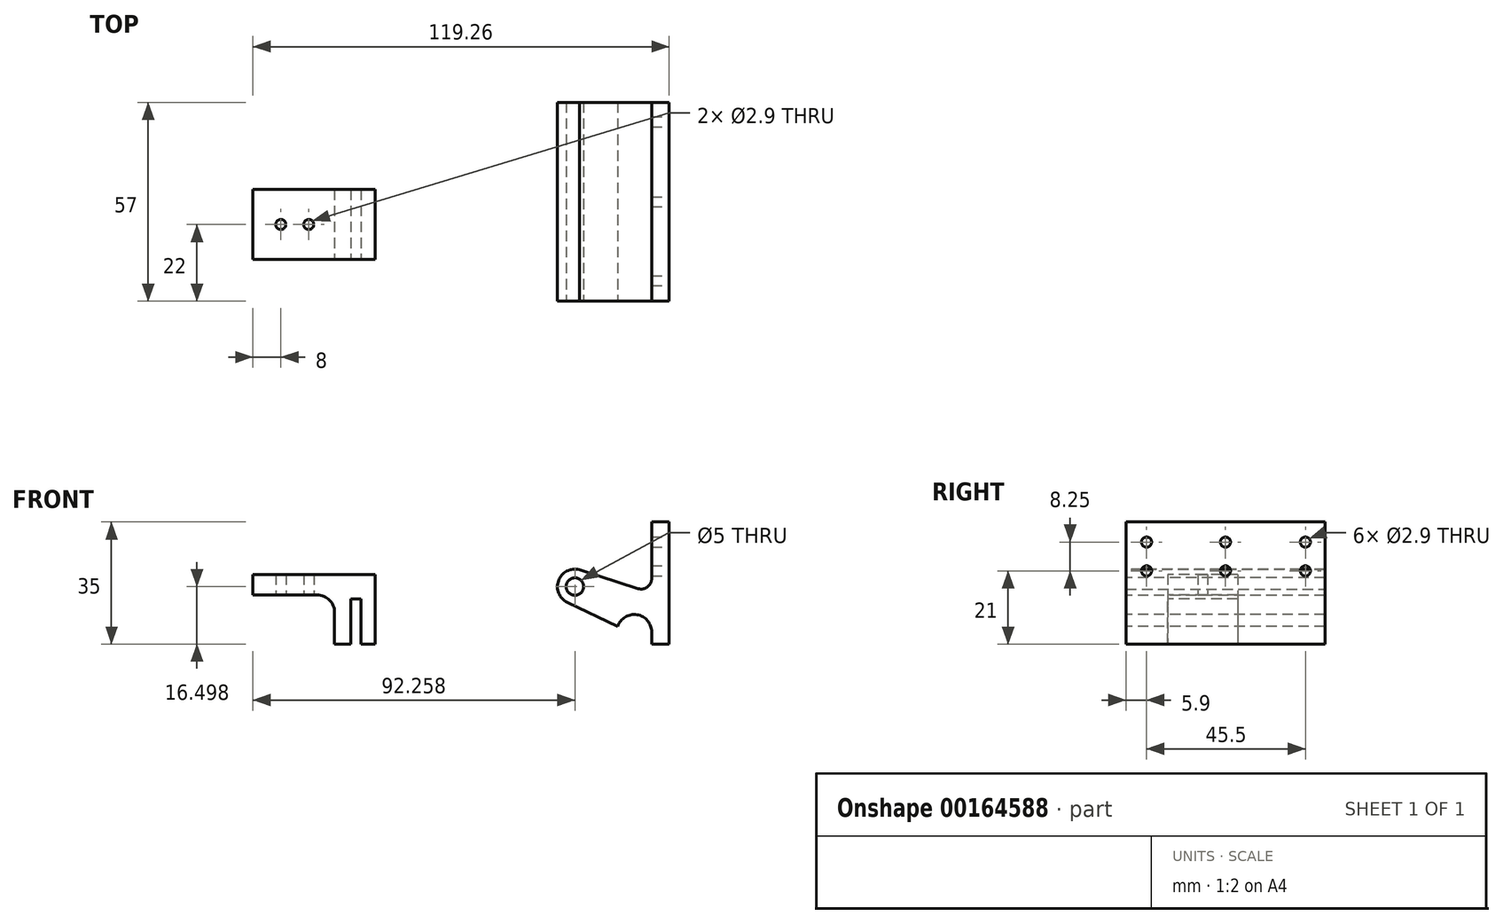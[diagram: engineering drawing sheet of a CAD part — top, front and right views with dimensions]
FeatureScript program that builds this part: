
annotation { "Feature Type Name" : "Feature", "Feature Type Description" : "" }
export const myFeature = defineFeature(function(context is Context, id is Id, definition is map)
    precondition{}
    {
        {
            var Q0;
            Q0=qCreatedBy(makeId("Top.planeOp"),FACE);
            var sketch = newSketch(context, id + "F0", { "sketchPlane" : qUnion([Q0])});
            skLineSegment(sketch, "E0.top", {"start": v(-55, -45) * mm, "end": v(-20, -45) * mm});
            skLineSegment(sketch, "E0.left", {"start": v(-55, -25) * mm, "end": v(-55, -45) * mm});
            skCircle(sketch, "E1", {"center": v(-47, -35) * mm, "radius": 1.45 * mm});
            skPoint(sketch, "E1.centerSnap0", {"position": v(-55, -22.5) * mm});
            skCircle(sketch, "E2", {"center": v(-39, -35) * mm, "radius": 1.45 * mm});
            skLineSegment(sketch, "E3.bottom", {"start": v(-55, -25) * mm, "end": v(-30, -25) * mm});
            skLineSegment(sketch, "E4.bottom", {"start": v(-55, -25) * mm, "end": v(-20, -25) * mm});
            skLineSegment(sketch, "E4.right", {"start": v(-20, -25) * mm, "end": v(-20, -45) * mm});
            skPoint(sketch, "E0.bottom.start.orphan", {"position": v(-55, 0) * mm});
            skPoint(sketch, "E5.orphan", {"position": v(0, -45) * mm});
            skSolve(sketch);
        }
        {
            var Q0;
            Q0=makeQuery(id+"F0.imprint","IMPRINT",FACE,{"disambiguationData":[TD([[makeQuery(id+"F0.imprint","IMPRINT",EDGE,{"derivedFrom":sQuery(id+"F0.wireOp",EDGE,"E1")}),-1.0]])]});
            extrude(context, id + "F1", {"entities" : qUnion([Q0]), "depth" : 20 * mm});
        }
        {
            var Q0;
            Q0=qCreatedBy(makeId("Top.planeOp"),FACE);
            var sketch = newSketch(context, id + "F2", { "sketchPlane" : qUnion([Q0])});
            skLineSegment(sketch, "E6.top", {"start": v(59.26, -57) * mm, "end": v(64.26, -57) * mm});
            skLineSegment(sketch, "E6.left", {"start": v(59.26, 0) * mm, "end": v(59.26, -57) * mm});
            skLineSegment(sketch, "E6.right", {"start": v(64.26, 0) * mm, "end": v(64.26, -57) * mm});
            skLineSegment(sketch, "E7", {"start": v(59.26, 0) * mm, "end": v(64.26, 0) * mm});
            skSolve(sketch);
        }
        {
            var Q0;
            Q0=qSketchRegion(id+"F2",true);
            extrude(context, id + "F3", {"entities" : qUnion([Q0]), "depth" : 35 * mm});
        }
        {
            var Q0;
            Q0=makeQuery(id+"F3.opExtrude","SWEPT_FACE",FACE,{"disambiguationData":[OSD([sQuery(id+"F2.wireOp",EDGE,"E6.right")])]});
            var sketch = newSketch(context, id + "F4", { "sketchPlane" : qUnion([Q0])});
            skCircle(sketch, "E8", {"center": v(-28.5, 21) * mm, "radius": 1.45 * mm});
            skCircle(sketch, "E9", {"center": v(-28.5, 29.25) * mm, "radius": 1.45 * mm});
            skCircle(sketch, "E10.1.0.0", {"center": v(-5.6, 29.25) * mm, "radius": 1.45 * mm});
            skCircle(sketch, "E10.1.0.1", {"center": v(-5.6, 21) * mm, "radius": 1.45 * mm});
            skLineSegment(sketch, "E10.direction1", {"start": v(-28.5, 29.25) * mm, "end": v(-5.6, 29.25) * mm, "construction": true});
            skCircle(sketch, "E11.1.0.0", {"center": v(-51.1, 29.25) * mm, "radius": 1.45 * mm});
            skCircle(sketch, "E11.1.0.1", {"center": v(-51.1, 21) * mm, "radius": 1.45 * mm});
            skLineSegment(sketch, "E11.direction1", {"start": v(-28.5, 29.25) * mm, "end": v(-51.1, 29.25) * mm, "construction": true});
            skSolve(sketch);
        }
        {
            var Q0;
            Q0=qSketchRegion(id+"F4",true);
            extrude(context, id + "F5", {"entities" : qUnion([Q0]), "operationType" : NewBodyOperationType.REMOVE, "oppositeDirection" : true, "depth" : 25 * mm});
        }
        {
            var Q0;
            Q0=makeQuery(id+"F1.opExtrude","SWEPT_FACE",FACE,{"disambiguationData":[OSD([sQuery(id+"F0.wireOp",EDGE,"E0.top")])]});
            var sketch = newSketch(context, id + "F6", { "sketchPlane" : qUnion([Q0])});
            skLineSegment(sketch, "E12.bottom", {"start": v(-24, 0) * mm, "end": v(-27, 0) * mm});
            skLineSegment(sketch, "E12.top", {"start": v(-24, 13) * mm, "end": v(-27, 13) * mm});
            skLineSegment(sketch, "E12.left", {"start": v(-24, 0) * mm, "end": v(-24, 13) * mm});
            skLineSegment(sketch, "E12.right", {"start": v(-27, 0) * mm, "end": v(-27, 13) * mm});
            skLineSegment(sketch, "E13.bottom", {"start": v(-31.6, 0) * mm, "end": v(-55, 0) * mm});
            skLineSegment(sketch, "E13.top", {"start": v(-31.6, 14.1) * mm, "end": v(-55, 14.1) * mm});
            skLineSegment(sketch, "E13.left", {"start": v(-31.6, 0) * mm, "end": v(-31.6, 14.1) * mm});
            skLineSegment(sketch, "E13.right", {"start": v(-55, 0) * mm, "end": v(-55, 14.1) * mm});
            skSolve(sketch);
        }
        {
            var Q0;
            Q0 = qSketchRegion(id + "F6", true);
            extrude(context, id + "F7", {"entities" : qUnion([Q0]), "operationType" : NewBodyOperationType.REMOVE, "oppositeDirection" : true, "depth" : 25 * mm});
        }
        {
            var Q0;
            Q0=makeQuery(id+"F7.boolean.opBoolean","COPY",EDGE,{"derivedFrom":makeQuery(id+"F7.opExtrude","SWEPT_EDGE",EDGE,{"disambiguationData":[OSD([sQuery(id+"F6.wireOp",EDGE,"E13.top"),sQuery(id+"F6.wireOp",EDGE,"E13.left")])]})});
            fillet(context, id + "F8", {"entities" : qUnion([Q0]), "radius" : 5 * mm, "tangentPropagation" : true, "allowEdgeOverflow" : false});
        }
        {
            var Q0;
            Q0=makeQuery(id+"F3.opExtrude","SWEPT_FACE",FACE,{"disambiguationData":[OSD([sQuery(id+"F2.wireOp",EDGE,"E6.top")])]});
            var sketch = newSketch(context, id + "F9", { "sketchPlane" : qUnion([Q0])});
            skArc(sketch, "E14", {"start": v(58.24, 0.47) * mm, "mid": v(56.6, 7.92) * mm, "end": v(49.52, 5.1) * mm});
            skLineSegment(sketch, "E15.left", {"start": v(54.26, 3.5) * mm, "end": v(54.26, 8.5) * mm});
            skLineSegment(sketch, "E15.right", {"start": v(32.26, 3.5) * mm, "end": v(32.26, 16.5) * mm, "construction": true});
            skCircle(sketch, "E16", {"center": v(37.26, 16.5) * mm, "radius": 2.5 * mm});
            skArc(sketch, "E17", {"start": v(39.03, 21.17) * mm, "mid": v(32.66, 18.46) * mm, "end": v(35.1, 11.99) * mm});
            skLineSegment(sketch, "E18", {"start": v(49.52, 5.1) * mm, "end": v(35.1, 11.99) * mm});
            skLineSegment(sketch, "E19", {"start": v(38.54, 21.33) * mm, "end": v(59.26, 14.68) * mm});
            skLineSegment(sketch, "E20", {"start": v(59.26, 0) * mm, "end": v(58.24, 0.47) * mm});
            skPoint(sketch, "E21.start.orphan", {"position": v(49.52, 7.03) * mm});
            skPoint(sketch, "E22.start.orphan", {"position": v(54.26, 11.27) * mm});
            skSolve(sketch);
        }
        {
            var Q0;
            Q0=makeQuery(id+"F9.imprint","IMPRINT",FACE,{"disambiguationData":[TD([[makeQuery(id+"F9.imprint","IMPRINT",EDGE,{"derivedFrom":sQuery(id+"F9.wireOp",EDGE,"E16")}),-1.0]])]});
            extrude(context, id + "F10", {"entities" : qUnion([Q0]), "operationType" : NewBodyOperationType.ADD, "oppositeDirection" : true, "depth" : 57 * mm});
        }
        {
            var Q0;
            Q0=makeQuery(id+"F10.opExtrude","SWEPT_EDGE",EDGE,{"disambiguationData":[OSD([sQuery(id+"F2.wireOp",EDGE,"E6.top"),sQuery(id+"F2.wireOp",EDGE,"E6.left"),sQuery(id+"F9.wireOp",EDGE,"E19")])]});
            fillet(context, id + "F11", {"entities" : qUnion([Q0]), "radius" : 3 * mm, "tangentPropagation" : true, "allowEdgeOverflow" : false});
        }
    });
